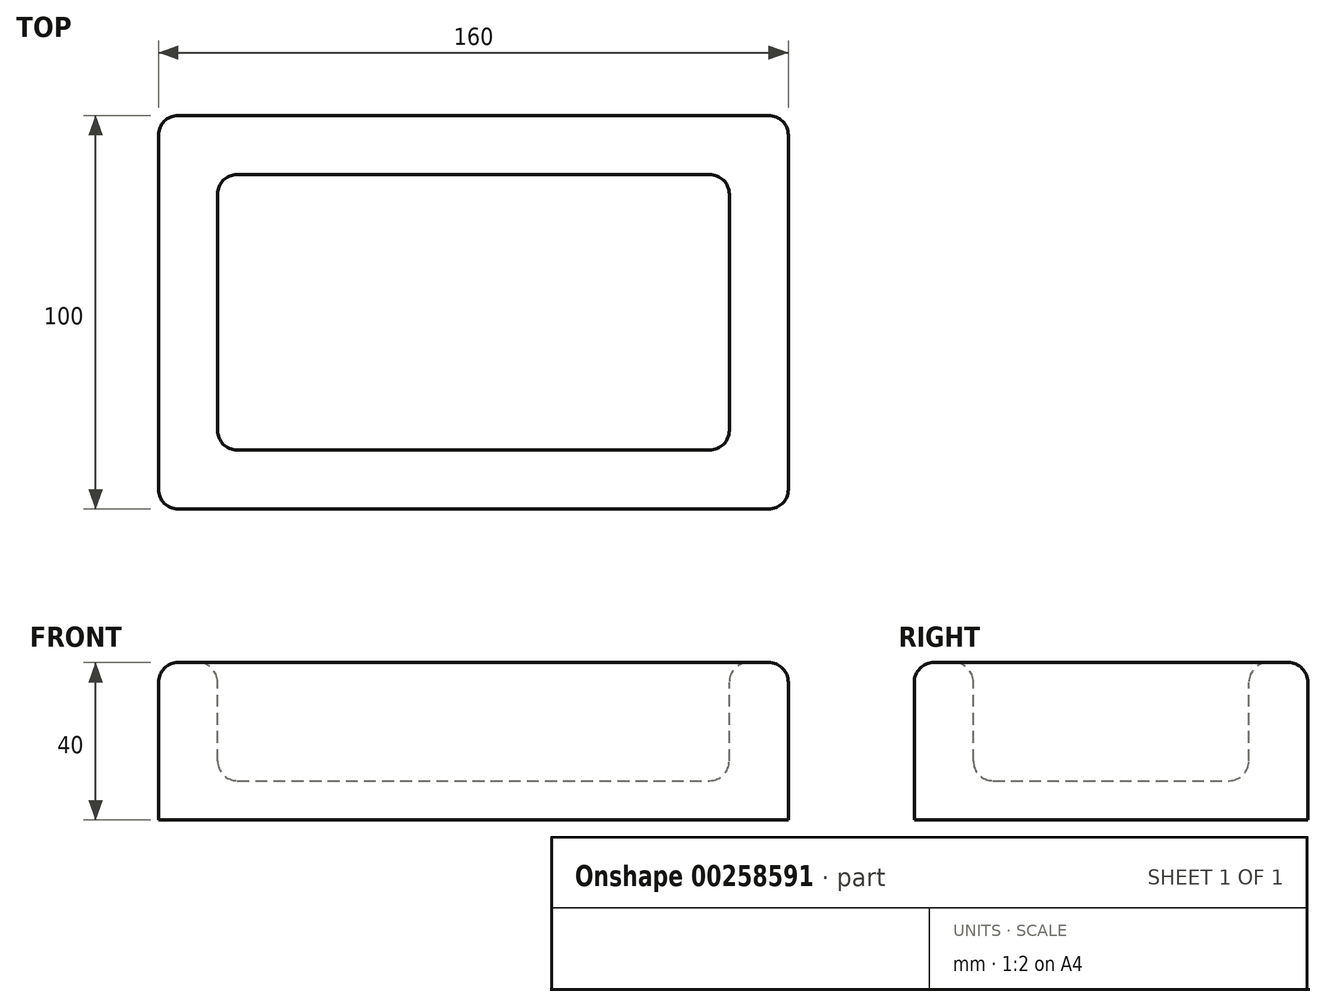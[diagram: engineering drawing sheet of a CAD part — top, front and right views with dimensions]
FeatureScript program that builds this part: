
annotation { "Feature Type Name" : "Feature", "Feature Type Description" : "" }
export const myFeature = defineFeature(function(context is Context, id is Id, definition is map)
    precondition{}
    {
        {
            var Q0;
            Q0=qCreatedBy(makeId("Top.planeOp"),FACE);
            var sketch = newSketch(context, id + "F0", { "sketchPlane" : qUnion([Q0])});
            skLineSegment(sketch, "E0.bottom", {"start": v(5, 0) * mm, "end": v(155, 0) * mm});
            skLineSegment(sketch, "E0.top", {"start": v(5, 100) * mm, "end": v(155, 100) * mm});
            skLineSegment(sketch, "E0.left", {"start": v(0, 5) * mm, "end": v(0, 95) * mm});
            skLineSegment(sketch, "E0.right", {"start": v(160, 5) * mm, "end": v(160, 95) * mm});
            skPoint(sketch, "E1.visualSharp", {"position": v(0, 100) * mm});
            skArc(sketch, "E1.filletArc", {"start": v(5, 100) * mm, "mid": v(1.46, 98.54) * mm, "end": v(0, 95) * mm});
            skPoint(sketch, "E2.visualSharp", {"position": v(160, 100) * mm});
            skArc(sketch, "E2.filletArc", {"start": v(160, 95) * mm, "mid": v(158.54, 98.54) * mm, "end": v(155, 100) * mm});
            skPoint(sketch, "E3.visualSharp", {"position": v(160, 0) * mm});
            skArc(sketch, "E3.filletArc", {"start": v(155, 0) * mm, "mid": v(158.54, 1.46) * mm, "end": v(160, 5) * mm});
            skPoint(sketch, "E4.visualSharp", {"position": v(0, 0) * mm});
            skArc(sketch, "E4.filletArc", {"start": v(0, 5) * mm, "mid": v(1.46, 1.46) * mm, "end": v(5, 0) * mm});
            skSolve(sketch);
        }
        {
            var Q0;
            Q0=makeQuery(id+"F0.imprint","IMPRINT",FACE,{"disambiguationData":[TD([[makeQuery(id+"F0.imprint","IMPRINT",EDGE,{"derivedFrom":sQuery(id+"F0.wireOp",EDGE,"E0.bottom")}),1.0]])]});
            extrude(context, id + "F1", {"entities" : qUnion([Q0]), "depth" : 40 * mm});
        }
        {
            var Q0;
            Q0=makeQuery(id+"F1.opExtrude","CAP_FACE",FACE,{"disambiguationData":[OSD([sQuery(id+"F0.wireOp",EDGE,"E0.bottom"),sQuery(id+"F0.wireOp",EDGE,"E0.top"),sQuery(id+"F0.wireOp",EDGE,"E0.left"),sQuery(id+"F0.wireOp",EDGE,"E0.right"),sQuery(id+"F0.wireOp",EDGE,"E1.filletArc"),sQuery(id+"F0.wireOp",EDGE,"E2.filletArc"),sQuery(id+"F0.wireOp",EDGE,"E3.filletArc"),sQuery(id+"F0.wireOp",EDGE,"E4.filletArc")])],"isStart":false});
            var sketch = newSketch(context, id + "F2", { "sketchPlane" : qUnion([Q0])});
            skLineSegment(sketch, "E5.0", {"start": v(5, 100) * mm, "end": v(155, 100) * mm});
            skArc(sketch, "E6.0", {"start": v(160, 95) * mm, "mid": v(158.54, 98.54) * mm, "end": v(155, 100) * mm});
            skLineSegment(sketch, "E6.1", {"start": v(160, 5) * mm, "end": v(160, 95) * mm});
            skLineSegment(sketch, "E6.2", {"start": v(5, 0) * mm, "end": v(155, 0) * mm});
            skArc(sketch, "E6.3", {"start": v(0, 5) * mm, "mid": v(1.46, 1.46) * mm, "end": v(5, 0) * mm});
            skLineSegment(sketch, "E6.4", {"start": v(0, 5) * mm, "end": v(0, 95) * mm});
            skArc(sketch, "E6.5", {"start": v(5, 100) * mm, "mid": v(1.46, 98.54) * mm, "end": v(0, 95) * mm});
            skPoint(sketch, "E6.6", {"position": v(158.54, 1.46) * mm});
            skLineSegment(sketch, "E7.0", {"start": v(20, 85) * mm, "end": v(140, 85) * mm});
            skLineSegment(sketch, "E7.1", {"start": v(15, 20) * mm, "end": v(15, 80) * mm});
            skLineSegment(sketch, "E7.2", {"start": v(20, 15) * mm, "end": v(140, 15) * mm});
            skLineSegment(sketch, "E7.3", {"start": v(145, 20) * mm, "end": v(145, 80) * mm});
            skPoint(sketch, "E8.visualSharp", {"position": v(15, 85) * mm});
            skArc(sketch, "E8.filletArc", {"start": v(20, 85) * mm, "mid": v(16.46, 83.54) * mm, "end": v(15, 80) * mm});
            skPoint(sketch, "E9.visualSharp", {"position": v(145, 85) * mm});
            skArc(sketch, "E9.filletArc", {"start": v(145, 80) * mm, "mid": v(143.54, 83.54) * mm, "end": v(140, 85) * mm});
            skPoint(sketch, "E10.visualSharp", {"position": v(145, 15) * mm});
            skArc(sketch, "E10.filletArc", {"start": v(140, 15) * mm, "mid": v(143.54, 16.46) * mm, "end": v(145, 20) * mm});
            skPoint(sketch, "E11.visualSharp", {"position": v(15, 15) * mm});
            skArc(sketch, "E11.filletArc", {"start": v(15, 20) * mm, "mid": v(16.46, 16.46) * mm, "end": v(20, 15) * mm});
            skSolve(sketch);
        }
        {
            var Q0;
            Q0=makeQuery(id+"F2.imprint","IMPRINT",FACE,{"disambiguationData":[TD([[makeQuery(id+"F2.imprint","IMPRINT",EDGE,{"derivedFrom":sQuery(id+"F2.wireOp",EDGE,"E7.0")}),-1.0]])]});
            extrude(context, id + "F3", {"entities" : qUnion([Q0]), "operationType" : NewBodyOperationType.REMOVE, "oppositeDirection" : true, "depth" : 30 * mm});
        }
        {
            var Q0;
            Q0=makeQuery(id+"F3.boolean.opBoolean","COPY",EDGE,{"derivedFrom":makeQuery(id+"F3.opExtrude","CAP_EDGE",EDGE,{"disambiguationData":[OSD([sQuery(id+"F2.wireOp",EDGE,"E7.0")])],"isStart":false})});
            var Q1;
            Q1=makeQuery(id+"F1.opExtrude","CAP_FACE",FACE,{"disambiguationData":[OSD([sQuery(id+"F0.wireOp",EDGE,"E0.bottom"),sQuery(id+"F0.wireOp",EDGE,"E0.top"),sQuery(id+"F0.wireOp",EDGE,"E0.left"),sQuery(id+"F0.wireOp",EDGE,"E0.right"),sQuery(id+"F0.wireOp",EDGE,"E1.filletArc"),sQuery(id+"F0.wireOp",EDGE,"E2.filletArc"),sQuery(id+"F0.wireOp",EDGE,"E3.filletArc"),sQuery(id+"F0.wireOp",EDGE,"E4.filletArc")])],"isStart":false});
            fillet(context, id + "F4", {"entities" : qUnion([Q0, Q1]), "radius" : 5 * mm, "tangentPropagation" : true, "allowEdgeOverflow" : false});
        }
    });
